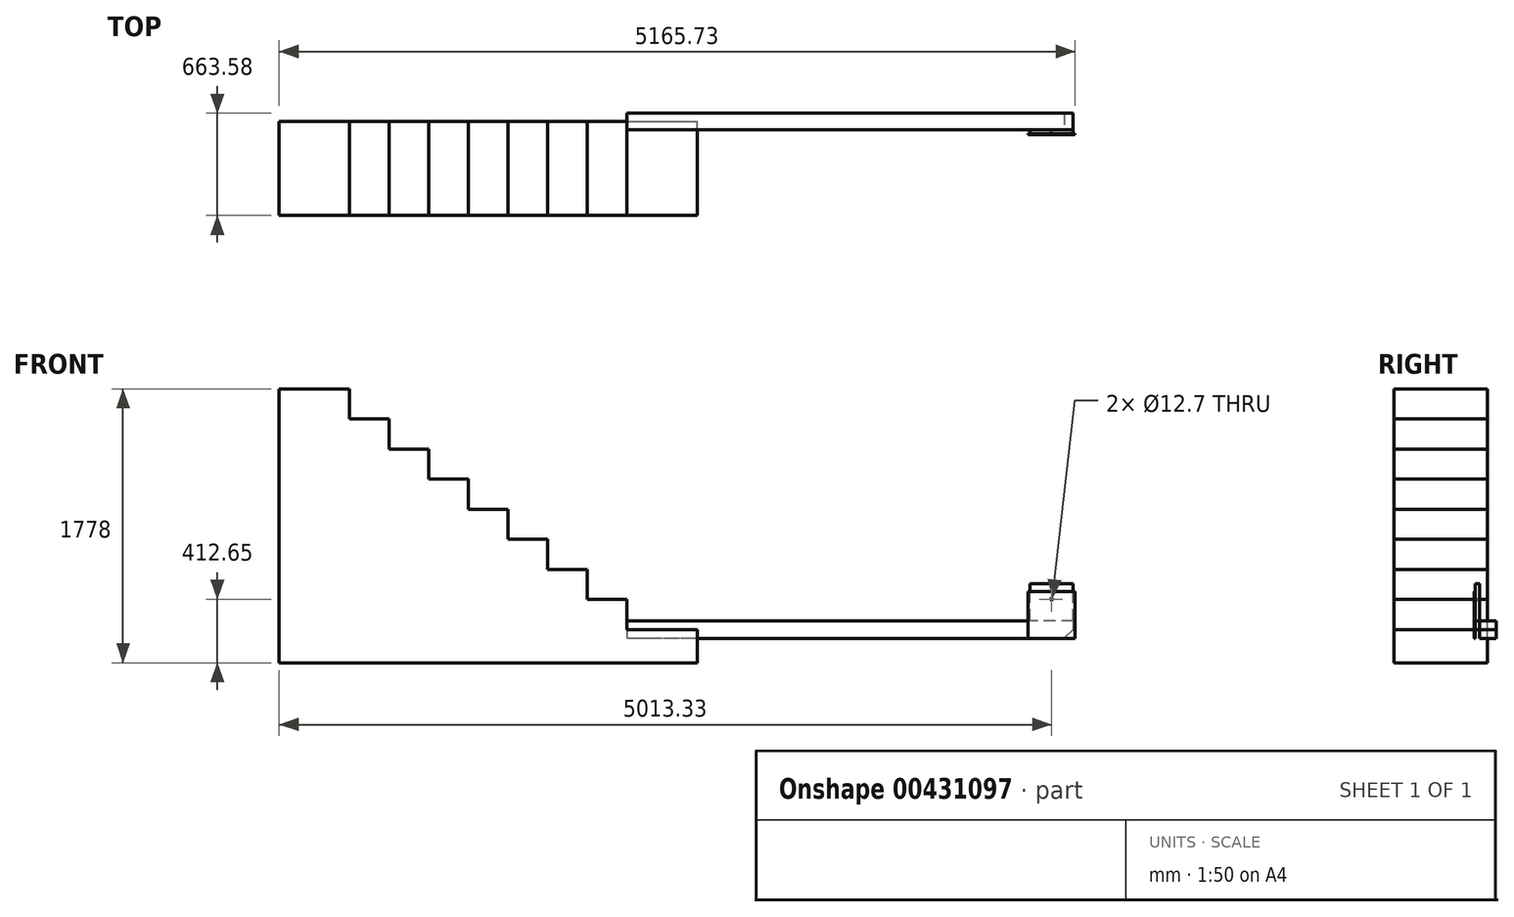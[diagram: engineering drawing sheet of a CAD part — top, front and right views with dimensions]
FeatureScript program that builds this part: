
annotation { "Feature Type Name" : "Feature", "Feature Type Description" : "" }
export const myFeature = defineFeature(function(context is Context, id is Id, definition is map)
    precondition{}
    {
        {
            var Q0;
            Q0=qCreatedBy(makeId("Front.planeOp"),FACE);
            var sketch = newSketch(context, id + "F0", { "sketchPlane" : qUnion([Q0])});
            skLineSegment(sketch, "E0", {"start": v(0, 0) * mm, "end": v(457.2, 0) * mm});
            skLineSegment(sketch, "E1", {"start": v(0, 0) * mm, "end": v(0, 195.28) * mm});
            skLineSegment(sketch, "E2", {"start": v(0, 195.28) * mm, "end": v(-257.18, 195.28) * mm});
            skLineSegment(sketch, "E3", {"start": v(-257.18, 195.28) * mm, "end": v(-257.18, 390.55) * mm});
            skLineSegment(sketch, "E4", {"start": v(-257.18, 390.55) * mm, "end": v(-514.35, 390.55) * mm});
            skLineSegment(sketch, "E5", {"start": v(-514.35, 390.55) * mm, "end": v(-514.35, 585.83) * mm});
            skLineSegment(sketch, "E6", {"start": v(-514.35, 585.83) * mm, "end": v(-771.53, 585.83) * mm});
            skLineSegment(sketch, "E7", {"start": v(-771.53, 585.83) * mm, "end": v(-771.53, 781.1) * mm});
            skLineSegment(sketch, "E8", {"start": v(-771.53, 781.1) * mm, "end": v(-1028.7, 781.1) * mm});
            skLineSegment(sketch, "E9", {"start": v(-1028.7, 781.1) * mm, "end": v(-1028.7, 976.38) * mm});
            skLineSegment(sketch, "E10", {"start": v(-1028.7, 976.38) * mm, "end": v(-1285.88, 976.38) * mm});
            skLineSegment(sketch, "E11", {"start": v(-1285.88, 976.38) * mm, "end": v(-1285.88, 1171.65) * mm});
            skLineSegment(sketch, "E12", {"start": v(-1285.88, 1171.65) * mm, "end": v(-1543.05, 1171.65) * mm});
            skLineSegment(sketch, "E13", {"start": v(-1543.05, 1171.65) * mm, "end": v(-1543.05, 1366.93) * mm});
            skLineSegment(sketch, "E14", {"start": v(-1543.05, 1366.93) * mm, "end": v(-1800.23, 1366.93) * mm});
            skLineSegment(sketch, "E15", {"start": v(-1800.23, 1366.93) * mm, "end": v(-1800.23, 1562.2) * mm});
            skLineSegment(sketch, "E16", {"start": v(-1800.23, 1562.2) * mm, "end": v(-2257.43, 1562.2) * mm});
            skLineSegment(sketch, "E17", {"start": v(-2257.43, 1562.2) * mm, "end": v(-2257.43, -215.8) * mm});
            skLineSegment(sketch, "E18", {"start": v(-2257.43, -215.8) * mm, "end": v(457.2, -215.8) * mm});
            skLineSegment(sketch, "E19", {"start": v(457.2, -215.8) * mm, "end": v(457.2, 0) * mm});
            skSolve(sketch);
        }
        {
            var Q0;
            Q0=makeQuery(id+"F0.imprint","IMPRINT",FACE,{"disambiguationData":[TD([[makeQuery(id+"F0.imprint","IMPRINT",EDGE,{"derivedFrom":sQuery(id+"F0.wireOp",EDGE,"E0")}),-1.0]])]});
            extrude(context, id + "F1", {"entities" : qUnion([Q0]), "depth" : 609.6 * mm});
        }
        {
            var Q0;
            Q0=qCreatedBy(makeId("Right.planeOp"),FACE);
            var sketch = newSketch(context, id + "F2", { "sketchPlane" : qUnion([Q0])});
            skLineSegment(sketch, "E20.bottom", {"start": v(53.98, 57.15) * mm, "end": v(-53.97, 57.15) * mm});
            skLineSegment(sketch, "E20.top", {"start": v(53.97, -57.15) * mm, "end": v(-53.98, -57.15) * mm});
            skLineSegment(sketch, "E20.left", {"start": v(53.98, 57.15) * mm, "end": v(53.98, -57.15) * mm});
            skLineSegment(sketch, "E20.right", {"start": v(-53.97, 57.15) * mm, "end": v(-53.98, -57.15) * mm});
            skPoint(sketch, "E20.middle", {"position": v(0, 0) * mm});
            skSolve(sketch);
        }
        {
            var Q0;
            Q0=makeQuery(id+"F2.imprint","IMPRINT",FACE,{"disambiguationData":[TD([[makeQuery(id+"F2.imprint","IMPRINT",EDGE,{"derivedFrom":sQuery(id+"F2.wireOp",EDGE,"E20.bottom")}),1.0]])]});
            extrude(context, id + "F3", {"entities" : qUnion([Q0]), "depth" : 2895.6 * mm});
        }
        {
            var Q0;
            Q0=makeQuery(id+"F3.opExtrude","SWEPT_FACE",FACE,{"disambiguationData":[OSD([sQuery(id+"F2.wireOp",EDGE,"E20.right")])]});
            var sketch = newSketch(context, id + "F4", { "sketchPlane" : qUnion([Q0])});
            skLineSegment(sketch, "E21.0", {"start": v(2895.6, -57.15) * mm, "end": v(0, -57.15) * mm});
            skPoint(sketch, "E22.0", {"position": v(2895.6, 0) * mm});
            skLineSegment(sketch, "E23.0", {"start": v(2895.6, 57.15) * mm, "end": v(2895.6, -57.15) * mm});
            skLineSegment(sketch, "E24", {"start": v(2895.6, 0) * mm, "end": v(2838.45, -57.15) * mm});
            skSolve(sketch);
        }
        {
            var Q0;
            {var subQ3=sQuery(id+"F4.wireOp",EDGE,"E24");Q0=makeQuery(id+"F4.imprint","IMPRINT",FACE,{"disambiguationData":[TD([[makeQuery(id+"F4.imprint","IMPRINT",EDGE,{"derivedFrom":subQ3}),1.0]])]});}
            extrude(context, id + "F5", {"entities" : qUnion([Q0]), "operationType" : NewBodyOperationType.REMOVE, "endBound" : BoundingType.UP_TO_NEXT, "oppositeDirection" : true, "depth" : 25.4 * mm});
        }
        {
            var Q0;
            Q0=makeQuery(id+"F3.opExtrude","SWEPT_FACE",FACE,{"disambiguationData":[OSD([sQuery(id+"F2.wireOp",EDGE,"E20.right")])]});
            var sketch = newSketch(context, id + "F6", { "sketchPlane" : qUnion([Q0])});
            skLineSegment(sketch, "E25.0", {"start": v(2838.45, -57.15) * mm, "end": v(0, -57.15) * mm});
            skLineSegment(sketch, "E26.0", {"start": v(2895.6, 57.15) * mm, "end": v(2895.6, 0) * mm});
            skLineSegment(sketch, "E27.bottom", {"start": v(2895.6, -57.15) * mm, "end": v(2616.2, -57.15) * mm});
            skLineSegment(sketch, "E27.top", {"start": v(2895.6, 298.45) * mm, "end": v(2616.2, 298.45) * mm});
            skLineSegment(sketch, "E27.left", {"start": v(2895.6, -57.15) * mm, "end": v(2895.6, 298.45) * mm});
            skLineSegment(sketch, "E27.right", {"start": v(2616.2, -57.15) * mm, "end": v(2616.2, 298.45) * mm});
            skPoint(sketch, "E28", {"position": v(2755.9, 196.85) * mm});
            skPoint(sketch, "E28.positionSnap0", {"position": v(2755.9, 298.45) * mm});
            skCircle(sketch, "E29", {"center": v(2755.9, 196.85) * mm, "radius": 6.35 * mm});
            skSolve(sketch);
        }
        {
            var Q0;
            {var subQ3=sQuery(id+"F6.wireOp",EDGE,"E27.top");Q0=makeQuery(id+"F6.imprint","IMPRINT",FACE,{"disambiguationData":[TD([[makeQuery(id+"F6.imprint","IMPRINT",EDGE,{"derivedFrom":subQ3}),1.0]])]});}
            var Q1;
            {var subQ0=makeQuery(id+"F5.boolean.opBoolean","COPY",EDGE,{"derivedFrom":makeQuery(id+"F5.opExtrude","CAP_EDGE",EDGE,{"disambiguationData":[OSD([sQuery(id+"F4.wireOp",EDGE,"E24")])],"isStart":true})});Q1=makeQuery(id+"F6.imprint","IMPRINT",FACE,{"disambiguationData":[TD([[makeQuery(id+"F6.imprint","IMPRINT",EDGE,{"derivedFrom":subQ0}),-1.0]])]});}
            var Q2;
            {var subQ1=makeQuery(id+"F5.boolean.opBoolean","COPY",EDGE,{"derivedFrom":makeQuery(id+"F5.opExtrude","CAP_EDGE",EDGE,{"disambiguationData":[OSD([sQuery(id+"F4.wireOp",EDGE,"E24")])],"isStart":true})});Q2=makeQuery(id+"F6.imprint","IMPRINT",FACE,{"disambiguationData":[TD([[makeQuery(id+"F6.imprint","IMPRINT",EDGE,{"derivedFrom":subQ1}),1.0]])]});}
            extrude(context, id + "F7", {"entities" : qUnion([Q0, Q1, Q2]), "depth" : 25.4 * mm});
        }
        {
            var Q0;
            Q0=makeQuery(id+"F7.opExtrude","CAP_FACE",FACE,{"disambiguationData":[OSD([sQuery(id+"F6.wireOp",EDGE,"E27.bottom"),sQuery(id+"F6.wireOp",EDGE,"E27.top"),sQuery(id+"F6.wireOp",EDGE,"E27.left"),sQuery(id+"F6.wireOp",EDGE,"E27.right"),sQuery(id+"F6.wireOp",EDGE,"E29")])],"isStart":false});
            var sketch = newSketch(context, id + "F8", { "sketchPlane" : qUnion([Q0])});
            skLineSegment(sketch, "E30.bottom", {"start": v(2603.5, 247.65) * mm, "end": v(2908.3, 247.65) * mm});
            skLineSegment(sketch, "E30.top", {"start": v(2603.5, -57.15) * mm, "end": v(2908.3, -57.15) * mm});
            skLineSegment(sketch, "E30.left", {"start": v(2603.5, 247.65) * mm, "end": v(2603.5, -57.15) * mm});
            skLineSegment(sketch, "E30.right", {"start": v(2908.3, 247.65) * mm, "end": v(2908.3, -57.15) * mm});
            skCircle(sketch, "E31.0", {"center": v(2755.9, 196.85) * mm, "radius": 6.35 * mm});
            skSolve(sketch);
        }
        {
            var Q0;
            {var subQ0=sQuery(id+"F8.wireOp",EDGE,"E30.left");Q0=makeQuery(id+"F8.imprint","IMPRINT",FACE,{"disambiguationData":[TD([[makeQuery(id+"F8.imprint","IMPRINT",EDGE,{"derivedFrom":subQ0}),1.0]])]});}
            var Q1;
            {var subQ0=sQuery(id+"F8.wireOp",EDGE,"E30.right");Q1=makeQuery(id+"F8.imprint","IMPRINT",FACE,{"disambiguationData":[TD([[makeQuery(id+"F8.imprint","IMPRINT",EDGE,{"derivedFrom":subQ0}),-1.0]])]});}
            var Q2;
            Q2=makeQuery(id+"F8.imprint","IMPRINT",FACE,{"disambiguationData":[TD([[makeQuery(id+"F8.imprint","IMPRINT",EDGE,{"derivedFrom":sQuery(id+"F8.wireOp",EDGE,"E31.0")}),-1.0]])]});
            extrude(context, id + "F9", {"entities" : qUnion([Q0, Q1, Q2]), "depth" : 6.35 * mm});
        }
    });
